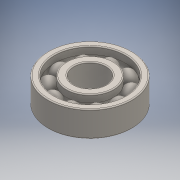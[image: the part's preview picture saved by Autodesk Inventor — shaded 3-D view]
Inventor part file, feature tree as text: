
AUTODESK INVENTOR PART (.ipt)
format: ipt  version: 2016 SP1 (Build 200210100, 210)  size: 532,480 bytes
history: native  units: mm
features: other x9, fillet x2, revolve x1
ambient origin geometry x8: Origin, YZ Plane, XZ Plane, XY Plane, X Axis, Y Axis, Z Axis, Center Point
bodies: Solid1 (feature_tree), Solid2 (feature_tree), Solid3 (feature_tree), Solid4 (feature_tree), Solid5 (feature_tree), Solid6 (feature_tree), Solid7 (feature_tree), Solid8 (feature_tree), Solid9 (feature_tree), Solid10 (feature_tree), Solid11 (feature_tree), Solid12 (feature_tree)
feature tree (12):
  revolve  "Revolve1"  [1 undecoded]
  other  "CirPattern1[1]"
  other  "CirPattern1[2]"
  other  "CirPattern1[3]"
  other  "CirPattern1[4]"
  other  "CirPattern1[5]"
  other  "CirPattern1[6]"
  other  "CirPattern1[7]"
  other  "CirPattern1[8]"
  other  "CirPattern1[9]"
  fillet  "Fillet1"  [1 undecoded]
  fillet  "Fillet2"  [1 undecoded]
note: 3 required parameter values undecoded (feature->parameter linkage not recoverable at this tier; creation-order binding heuristic only, values carry confidence <= 0.55)
